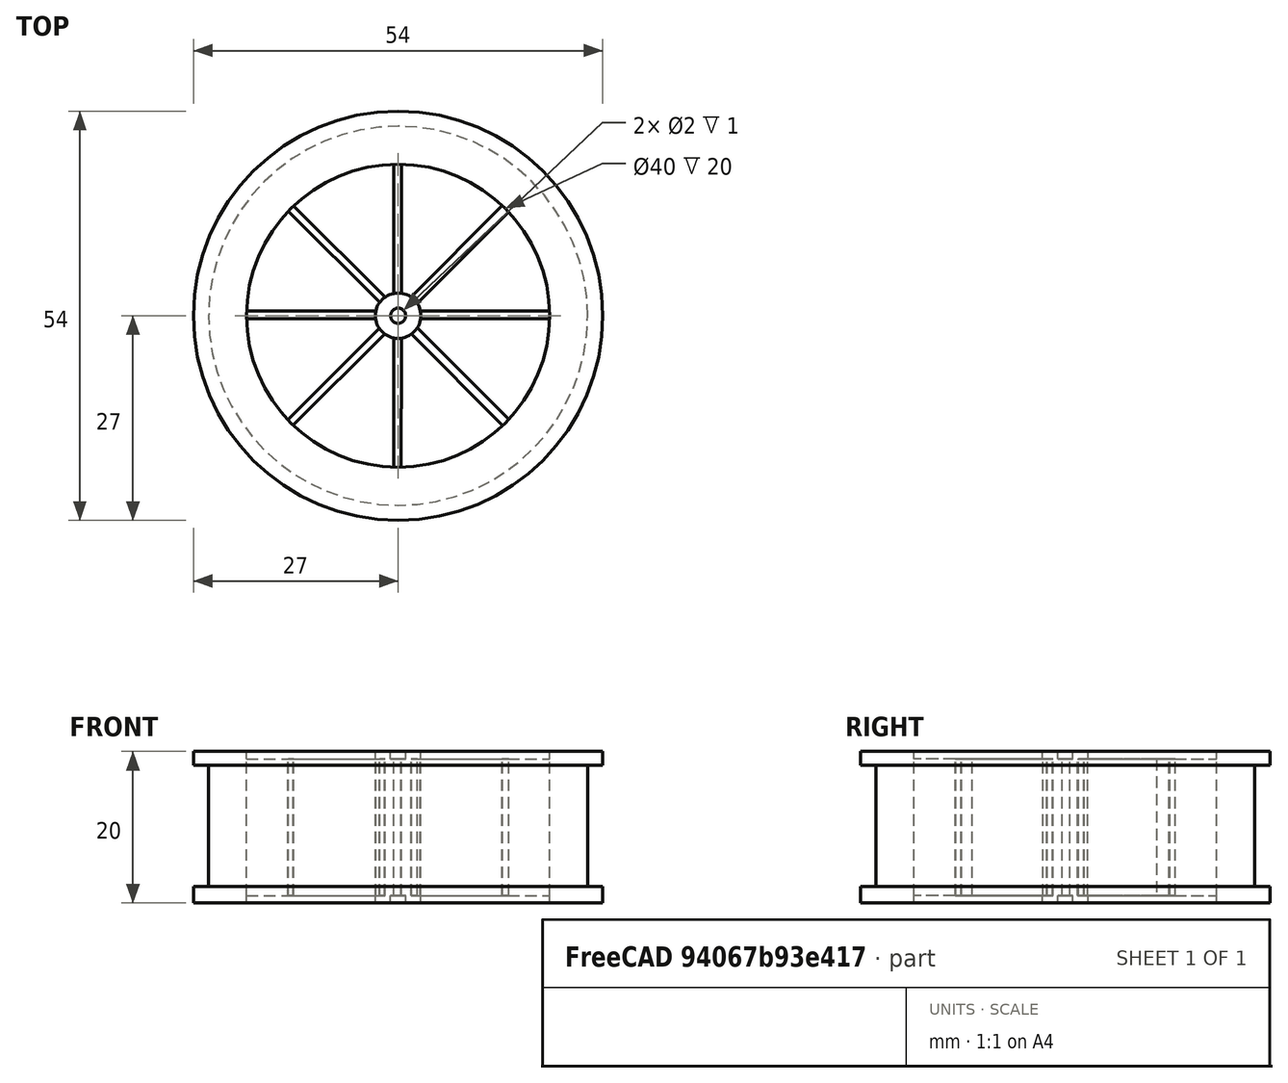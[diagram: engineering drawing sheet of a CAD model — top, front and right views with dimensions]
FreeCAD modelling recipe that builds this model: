
FCSTD DOCUMENT  (FreeCAD 0.21R33771 (Git))
Label: Rueda
License: All rights reserved
LicenseURL: http://en.wikipedia.org/wiki/All_rights_reserved
objects: Part::Box×8, Part::FeaturePython×4, Part::Cut×2, Part::MultiFuse×2, App::MeasureDistance×1
note: 16 computed .brp shape members not serialized (recipe doc carries the construction recipe); baked Part::Feature solids carry a one-line shape summary decoded from their .brp

FEATURE [Part::FeaturePython] Tube  # WARN: FeaturePython — macro-defined, semantics opaque (R4)
  AttacherType = Attacher::AttachEngine3D
  Height = 20
  InnerRadius = 15
  OuterRadius = 27
FEATURE [Part::FeaturePython] Tube001  # WARN: FeaturePython — macro-defined, semantics opaque (R4)
  AttacherType = Attacher::AttachEngine3D
  Height = 16
  InnerRadius = 25
  OuterRadius = 40
  Placement = pos=(0,0,2.2) rot=(0,0,1;0rad)
FEATURE [Part::Cut] Cut
  Base = -> Tube
  Tool = -> Tube001
FEATURE [Part::FeaturePython] Tube002  # WARN: FeaturePython — macro-defined, semantics opaque (R4)
  AttacherType = Attacher::AttachEngine3D
  Height = 25
  InnerRadius = 2
  OuterRadius = 20
  Placement = pos=(0,0,-2.6) rot=(0,0,1;0rad)
FEATURE [Part::Cut] Cut001
  Base = -> Cut
  Tool = -> Tube002
FEATURE [Part::FeaturePython] Tube003  # WARN: FeaturePython — macro-defined, semantics opaque (R4)
  AttacherType = Attacher::AttachEngine3D
  Height = 20
  InnerRadius = 1
  OuterRadius = 3
FEATURE [Part::Box] Box  label="Cubo"
  AttacherType = Attacher::AttachEngine3D
  Height = 18
  Length = 20
  Placement = pos=(0.75,-1.25,1) rot=(0,0,-1;0.785398rad)
  Width = 1
FEATURE [Part::Box] Box001  label="Cubo001"
  AttacherType = Attacher::AttachEngine3D
  Height = 18
  Length = 45
  Placement = pos=(-16.81,-17.43,1) rot=(0,0,1;0.785398rad)
  Width = 1
FEATURE [Part::Box] Box002  label="Cubo002"
  AttacherType = Attacher::AttachEngine3D
  Height = 18
  Length = 35
  Placement = pos=(0.42,-12.28,1) rot=(0,0,1;1.5708rad)
  Width = 1
FEATURE [Part::Box] Box003  label="Cubo003"
  AttacherType = Attacher::AttachEngine3D
  Height = 18
  Length = 20
  Placement = pos=(2.23,1.34,1) rot=(0,0,1;0.785398rad)
  Width = 1
FEATURE [Part::Box] Box004  label="Cubo004"
  AttacherType = Attacher::AttachEngine3D
  Height = 18
  Length = 45
  Placement = pos=(-22.4,-0.4,1) rot=(0,0,1;0rad)
  Width = 1
FEATURE [Part::Box] Box005  label="Cubo005"
  AttacherType = Attacher::AttachEngine3D
  Height = 18
  Length = 20
  Placement = pos=(1.8,-0.4,1) rot=(0,0,1;0rad)
  Width = 1
FEATURE [Part::Box] Box006  label="Cubo006"
  AttacherType = Attacher::AttachEngine3D
  Height = 18
  Length = 35
  Placement = pos=(-0.6,12,1) rot=(0,0,-1;1.5708rad)
  Width = 1
FEATURE [Part::Box] Box007  label="Cubo007"
  AttacherType = Attacher::AttachEngine3D
  Height = 18
  Length = 45
  Placement = pos=(-16.7068,16.0068,1) rot=(0,0,-1;0.785398rad)
  Width = 1
FEATURE [Part::MultiFuse] Fusion
  Shapes = -> [Box007,Box006,Box005,Box004,Box003,Box002,Box001,Box,Tube003]
FEATURE [Part::MultiFuse] Fusion001
  Shapes = -> [Cut001,Fusion]
FEATURE [App::MeasureDistance] Distance  label="Distance: 16,00 mm"
  Distance = 16
  P1 = (27,-6.6e-15,2.2)
  P2 = (27,-6.6e-15,18.2)
